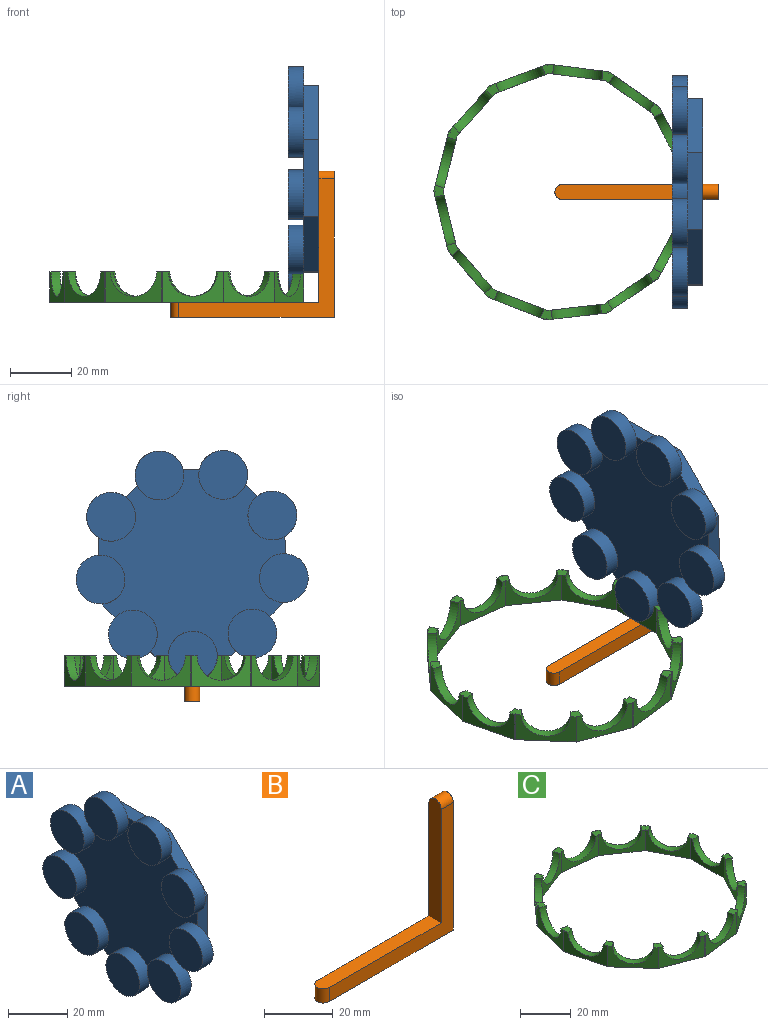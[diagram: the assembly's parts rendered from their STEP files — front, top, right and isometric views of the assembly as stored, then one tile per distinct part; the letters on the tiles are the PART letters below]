
ASSEMBLY  parts=3 mates=2
PART A: 37 faces, bbox 10x76.1x75.2 mm
  f0: cylinder r=8mm len=16mm, axis (1,0,0), area 251.3mm2, adj f1,f2,f3
  f1: plane 16x16mm, normal (-1,0,0), area 201.1mm2, adj f0
  f2: plane 16x8mm, normal (1,0,0), area 100.5mm2, adj f0,f35
  f3: plane 61x61mm, normal (-1,0,0), area 2109.6mm2, adj f0,f4,f7,f10,f13,f16,f19,f22
  f4: cylinder r=8mm len=16mm, axis (1,0,0), area 251.3mm2, adj f3,f5,f6
  f5: plane 16x16mm, normal (-1,0,0), area 201.1mm2, adj f4
  f6: plane 13.57x13.57mm, normal (1,0,0), area 98.7mm2, adj f4,f34
  f7: cylinder r=8mm len=16mm, axis (1,0,0), area 251.3mm2, adj f3,f8,f9
  f8: plane 16x16mm, normal (-1,0,0), area 201.1mm2, adj f7
  f9: plane 15.99x8.2mm, normal (1,0,0), area 93.3mm2, adj f7,f33,f34
  f10: cylinder r=8mm len=16mm, axis (1,0,0), area 251.3mm2, adj f3,f11,f12
  f11: plane 16x16mm, normal (-1,0,0), area 201.1mm2, adj f10
  f12: plane 14.88x12.87mm, normal (1,0,0), area 89mm2, adj f10,f32,f33
  f13: cylinder r=8mm len=16mm, axis (1,0,0), area 251.3mm2, adj f3,f14,f15
  f14: plane 16x16mm, normal (-1,0,0), area 201.1mm2, adj f13
  f15: plane 15.79x11.26mm, normal (1,0,0), area 87.1mm2, adj f13,f31,f32
  f16: cylinder r=8mm len=16mm, axis (1,0,0), area 251.3mm2, adj f3,f17,f18
  f17: plane 16x16mm, normal (-1,0,0), area 201.1mm2, adj f16
  f18: plane 15.79x11.26mm, normal (1,0,0), area 87.1mm2, adj f16,f30,f31
  f19: cylinder r=8mm len=16mm, axis (1,0,0), area 251.3mm2, adj f3,f20,f21
  f20: plane 16x16mm, normal (-1,0,0), area 201.1mm2, adj f19
  f21: plane 14.88x12.87mm, normal (1,0,0), area 89mm2, adj f19,f29,f30
  f22: cylinder r=8mm len=16mm, axis (1,0,0), area 251.3mm2, adj f3,f23,f24
  f23: plane 16x16mm, normal (-1,0,0), area 201.1mm2, adj f22
  f24: plane 15.99x8.2mm, normal (1,0,0), area 93.3mm2, adj f22,f28,f29
  f25: cylinder r=8mm len=16mm, axis (1,0,0), area 251.3mm2, adj f3,f26,f27
  f26: plane 16x16mm, normal (-1,0,0), area 201.1mm2, adj f25
  f27: plane 13.57x13.57mm, normal (1,0,0), area 98.7mm2, adj f25,f28
  f28: plane 17.87x17.87mm, normal (0,0.71,-0.71), area 126.3mm2, adj f3,f24,f27,f29,f35,f36
  f29: plane 25.27x5mm, normal (0,1,0), area 126.3mm2, adj f3,f21,f24,f28,f30,f36
  f30: plane 17.87x17.87mm, normal (0,0.71,0.71), area 126.3mm2, adj f3,f18,f21,f29,f31,f36
  f31: plane 25.27x5mm, normal (0,0,1), area 126.3mm2, adj f3,f15,f18,f30,f32,f36
  f32: plane 17.87x17.87mm, normal (0,-0.71,0.71), area 126.3mm2, adj f3,f12,f15,f31,f33,f36
  f33: plane 25.27x5mm, normal (0,-1,0), area 126.3mm2, adj f3,f9,f12,f32,f34,f36
  f34: plane 17.87x17.87mm, normal (0,-0.71,-0.71), area 126.3mm2, adj f3,f6,f9,f33,f35,f36
  f35: plane 25.27x5mm, normal (0,0,-1), area 126.3mm2, adj f2,f3,f28,f34,f36
  f36: plane 61x61mm, normal (1,0,0), area 3082.4mm2, adj f28,f29,f30,f31,f32,f33,f34,f35
PART B: 8 faces, bbox 53.5x5x48 mm
  f0: plane 43x5mm, normal (-1,0,0), area 212.3mm2, adj f1,f4,f5,f7
  f1: plane 48.5x5mm, normal (0,0,1), area 239.8mm2, adj f0,f4,f5,f6
  f2: plane 53.5x5mm, normal (0,0,-1), area 264.8mm2, adj f3,f4,f5,f6
  f3: plane 48x5mm, normal (1,0,0), area 237.3mm2, adj f2,f4,f5,f7
  f4: plane 51x45.5mm, normal (0,-1,0), area 457.5mm2, adj f0,f1,f2,f3,f6,f7
  f5: plane 51x45.5mm, normal (0,1,0), area 457.5mm2, adj f0,f1,f2,f3,f6,f7
  f6: cylinder r=2.5mm len=5mm, axis (0,0,1), area 39.3mm2, adj f1,f2,f4,f5
  f7: cylinder r=2.5mm len=5mm, axis (1,0,0), area 39.3mm2, adj f0,f3,f4,f5
PART C: 79 faces, bbox 83.2x83.8x10 mm
  f0: plane 10x0.43mm, normal (0,-1,0), area 4.3mm2, adj f5,f6,f7,f76
  f1: plane 18.73x10mm, normal (-1,0,0), area 84.3mm2, adj f3,f4,f5,f6,f9,f10
  f2: plane 10x0.43mm, normal (0,1,0), area 4.3mm2, adj f3,f6,f7,f8
  f3: plane 3.78x3.59mm, normal (0,0,1), area 9.8mm2, adj f1,f2,f4,f7,f8,f9,f13,f14
  f4: cylinder r=8.1mm len=16.2mm, axis (1,0,0), area 76.3mm2, adj f1,f3,f5,f7
  f5: plane 3.78x3.59mm, normal (0,0,1), area 9.8mm2, adj f0,f1,f4,f7,f10,f76,f77,f78
  f6: plane 83.81x83.2mm, normal (0,0,-1), area 758.8mm2, adj f0,f1,f2,f7,f8,f9,f10,f11
  f7: plane 20x10mm, normal (1,0,0), area 96.9mm2, adj f0,f2,f3,f4,f5,f6
  f8: plane 10x0.38mm, normal (0.46,-0.89,0), area 4.3mm2, adj f2,f3,f6,f14
  f9: plane 16.59x10mm, normal (-0.89,-0.46,0), area 84.3mm2, adj f1,f3,f6,f12,f13,f16
  f10: plane 16.59x10mm, normal (-0.89,0.46,0), area 84.3mm2, adj f1,f5,f6,f70,f72,f77
  f11: plane 10x0.38mm, normal (-0.46,0.89,0), area 4.3mm2, adj f6,f12,f14,f15
  f12: plane 4.31x4.29mm, normal (0,0,1), area 9.8mm2, adj f9,f11,f13,f14,f15,f16,f19,f20
  f13: cylinder r=8.1mm len=15.74mm, axis (0.89,0.46,0), area 76.3mm2, adj f3,f9,f12,f14
  f14: plane 17.71x10mm, normal (0.89,0.46,0), area 96.9mm2, adj f3,f6,f8,f11,f12,f13
  f15: plane 10x0.35mm, normal (0.82,-0.57,0), area 4.3mm2, adj f6,f11,f12,f20
  f16: plane 15.42x10.64mm, normal (-0.57,-0.82,0), area 84.3mm2, adj f6,f9,f12,f18,f19,f22
  f17: plane 10x0.35mm, normal (-0.82,0.57,0), area 4.3mm2, adj f6,f18,f20,f21
  f18: plane 4x3.85mm, normal (0,0,1), area 9.8mm2, adj f16,f17,f19,f20,f21,f22,f25,f26
  f19: cylinder r=8.1mm len=15.04mm, axis (0.57,0.82,0), area 76.3mm2, adj f12,f16,f18,f20
  f20: plane 16.46x11.36mm, normal (0.57,0.82,0), area 96.9mm2, adj f6,f12,f15,f17,f18,f19
  f21: plane 10x0.43mm, normal (0.99,-0.12,0), area 4.3mm2, adj f6,f17,f18,f26
  f22: plane 18.6x10mm, normal (-0.12,-0.99,0), area 84.3mm2, adj f6,f16,f18,f24,f25,f28
  f23: plane 10x0.43mm, normal (-0.99,0.12,0), area 4.3mm2, adj f6,f24,f26,f27
  f24: plane 3.87x3.5mm, normal (0,0,1), area 9.8mm2, adj f22,f23,f25,f26,f27,f28,f31,f32
  f25: cylinder r=8.1mm len=16.44mm, axis (0.12,0.99,0), area 76.3mm2, adj f18,f22,f24,f26
  f26: plane 19.85x10mm, normal (0.12,0.99,0), area 96.9mm2, adj f6,f18,f21,f23,f24,f25
  f27: plane 10x0.4mm, normal (0.94,0.35,0), area 4.3mm2, adj f6,f23,f24,f32
  f28: plane 17.52x10mm, normal (0.35,-0.94,0), area 84.3mm2, adj f6,f22,f24,f30,f31,f34
  f29: plane 10x0.4mm, normal (-0.94,-0.35,0), area 4.3mm2, adj f6,f30,f32,f33
  f30: plane 4.27x4.2mm, normal (0,0,1), area 9.8mm2, adj f28,f29,f31,f32,f33,f34,f37,f38
  f31: cylinder r=8.1mm len=16.21mm, axis (-0.35,0.94,0), area 76.3mm2, adj f24,f28,f30,f32
  f32: plane 18.7x10mm, normal (-0.35,0.94,0), area 96.9mm2, adj f6,f24,f27,f29,f30,f31
  f33: plane 10x0.32mm, normal (0.66,0.75,0), area 4.3mm2, adj f6,f29,f30,f38
  f34: plane 14.02x12.42mm, normal (0.75,-0.66,0), area 84.3mm2, adj f6,f28,f30,f36,f37,f40
  f35: plane 10x0.32mm, normal (-0.66,-0.75,0), area 4.3mm2, adj f6,f36,f38,f39
  f36: plane 4.17x4.06mm, normal (0,0,1), area 9.8mm2, adj f34,f35,f37,f38,f39,f40,f43,f44
  f37: cylinder r=8.1mm len=14.12mm, axis (-0.75,0.66,0), area 76.3mm2, adj f30,f34,f36,f38
  f38: plane 14.97x13.26mm, normal (-0.75,0.66,0), area 96.9mm2, adj f6,f30,f33,f35,f36,f37
  f39: plane 10x0.42mm, normal (0.24,0.97,0), area 4.3mm2, adj f6,f35,f36,f44
  f40: plane 18.19x10mm, normal (0.97,-0.24,0), area 84.3mm2, adj f6,f34,f36,f42,f43,f46
  f41: plane 10x0.42mm, normal (-0.24,-0.97,0), area 4.3mm2, adj f6,f42,f44,f45
  f42: plane 3.89x3.37mm, normal (0,0,1), area 9.8mm2, adj f40,f41,f43,f44,f45,f46,f49,f50
  f43: cylinder r=8.1mm len=16.45mm, axis (-0.97,0.24,0), area 76.3mm2, adj f36,f40,f42,f44
  f44: plane 19.42x10mm, normal (-0.97,0.24,0), area 96.9mm2, adj f6,f36,f39,f41,f42,f43
  f45: plane 10x0.42mm, normal (-0.24,0.97,0), area 4.3mm2, adj f6,f41,f42,f50
  f46: plane 18.19x10mm, normal (0.97,0.24,0), area 84.3mm2, adj f6,f40,f42,f48,f49,f52
  f47: plane 10x0.42mm, normal (0.24,-0.97,0), area 4.3mm2, adj f6,f48,f50,f51
  f48: plane 4.17x4.06mm, normal (0,0,1), area 9.8mm2, adj f46,f47,f49,f50,f51,f52,f55,f56
  f49: cylinder r=8.1mm len=16.45mm, axis (-0.97,-0.24,0), area 76.3mm2, adj f42,f46,f48,f50
  f50: plane 19.42x10mm, normal (-0.97,-0.24,0), area 96.9mm2, adj f6,f42,f45,f47,f48,f49
  f51: plane 10x0.32mm, normal (-0.66,0.75,0), area 4.3mm2, adj f6,f47,f48,f56
  f52: plane 14.02x12.42mm, normal (0.75,0.66,0), area 84.3mm2, adj f6,f46,f48,f54,f55,f58
  f53: plane 10x0.32mm, normal (0.66,-0.75,0), area 4.3mm2, adj f6,f54,f56,f57
  f54: plane 4.27x4.2mm, normal (0,0,1), area 9.8mm2, adj f52,f53,f55,f56,f57,f58,f61,f62
  f55: cylinder r=8.1mm len=14.12mm, axis (-0.75,-0.66,0), area 76.3mm2, adj f48,f52,f54,f56
  f56: plane 14.97x13.26mm, normal (-0.75,-0.66,0), area 96.9mm2, adj f6,f48,f51,f53,f54,f55
  f57: plane 10x0.4mm, normal (-0.94,0.35,0), area 4.3mm2, adj f6,f53,f54,f62
  f58: plane 17.52x10mm, normal (0.35,0.94,0), area 84.3mm2, adj f6,f52,f54,f60,f61,f64
  f59: plane 10x0.4mm, normal (0.94,-0.35,0), area 4.3mm2, adj f6,f60,f62,f63
  f60: plane 3.87x3.5mm, normal (0,0,1), area 9.8mm2, adj f58,f59,f61,f62,f63,f64,f67,f68
  f61: cylinder r=8.1mm len=16.21mm, axis (-0.35,-0.94,0), area 76.3mm2, adj f54,f58,f60,f62
  f62: plane 18.7x10mm, normal (-0.35,-0.94,0), area 96.9mm2, adj f6,f54,f57,f59,f60,f61
  f63: plane 10x0.43mm, normal (-0.99,-0.12,0), area 4.3mm2, adj f6,f59,f60,f68
  f64: plane 18.6x10mm, normal (-0.12,0.99,0), area 84.3mm2, adj f6,f58,f60,f66,f67,f70
  f65: plane 10x0.43mm, normal (0.99,0.12,0), area 4.3mm2, adj f6,f66,f68,f69
  f66: plane 4x3.85mm, normal (0,0,1), area 9.8mm2, adj f64,f65,f67,f68,f69,f70,f73,f74
  f67: cylinder r=8.1mm len=16.44mm, axis (0.12,-0.99,0), area 76.3mm2, adj f60,f64,f66,f68
  f68: plane 19.85x10mm, normal (0.12,-0.99,0), area 96.9mm2, adj f6,f60,f63,f65,f66,f67
  f69: plane 10x0.35mm, normal (-0.82,-0.57,0), area 4.3mm2, adj f6,f65,f66,f74
  f70: plane 15.42x10.64mm, normal (-0.57,0.82,0), area 84.3mm2, adj f6,f10,f64,f66,f72,f73
  f71: plane 10x0.35mm, normal (0.82,0.57,0), area 4.3mm2, adj f6,f72,f74,f75
  f72: plane 4.31x4.29mm, normal (0,0,1), area 9.8mm2, adj f10,f70,f71,f73,f74,f75,f77,f78
  f73: cylinder r=8.1mm len=15.04mm, axis (0.57,-0.82,0), area 76.3mm2, adj f66,f70,f72,f74
  f74: plane 16.46x11.36mm, normal (0.57,-0.82,0), area 96.9mm2, adj f6,f66,f69,f71,f72,f73
  f75: plane 10x0.38mm, normal (-0.46,-0.89,0), area 4.3mm2, adj f6,f71,f72,f78
  f76: plane 10x0.38mm, normal (0.46,0.89,0), area 4.3mm2, adj f0,f5,f6,f78
  f77: cylinder r=8.1mm len=15.74mm, axis (0.89,-0.46,0), area 76.3mm2, adj f5,f10,f72,f78
  f78: plane 17.71x10mm, normal (0.89,-0.46,0), area 96.9mm2, adj f5,f6,f72,f75,f76,f77
PLACE A rot(axis=(-1,0,0),0.5deg) t=(7.21,-5.54,-15.21)mm
PLACE B t=(7.21,-5.3,-15.21)mm fixed
PLACE C rot(axis=(0,0,1),82.7deg) t=(7.21,-5.3,-15.21)mm
MATE revolute C.f6 <-> B.f6  axis (0,0,-1) through (7.21,-5.3,-25.21)mm
MATE revolute A.f36 <-> B.f7  axis (1,0,0) through (53.21,-5.3,15.28)mm
